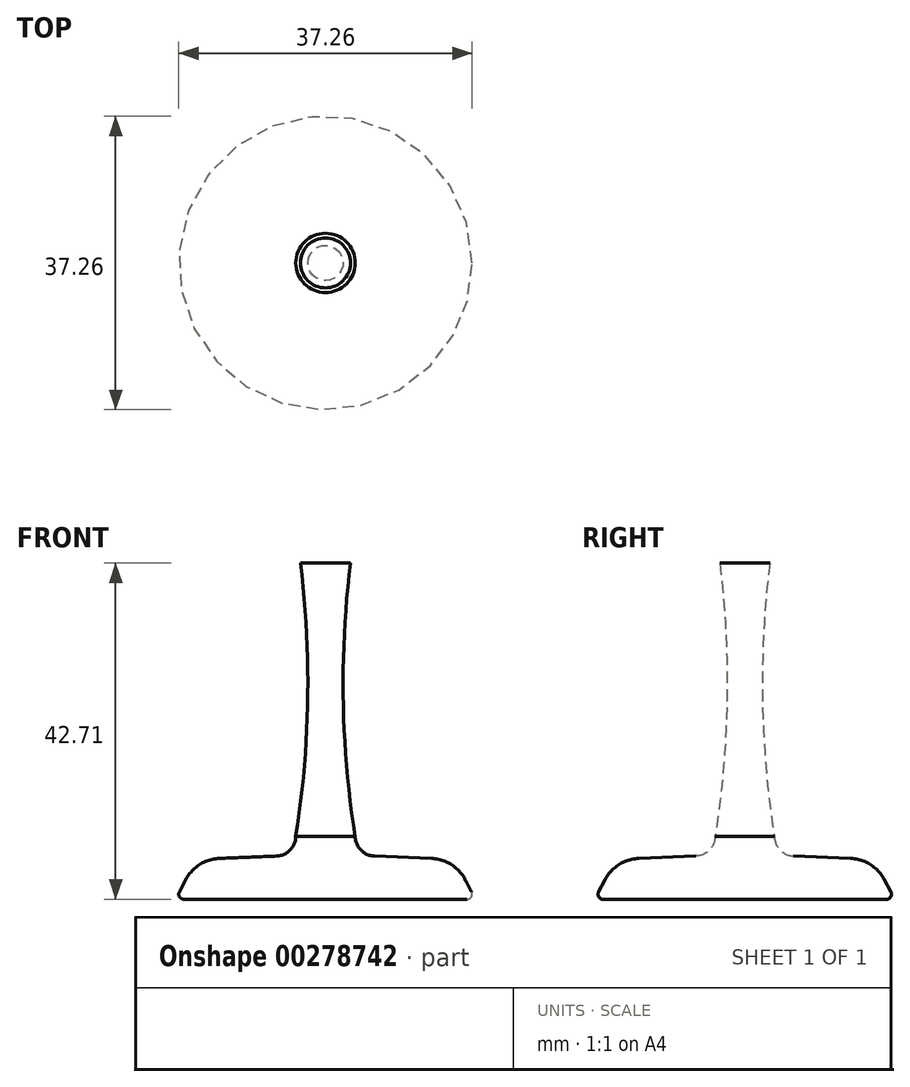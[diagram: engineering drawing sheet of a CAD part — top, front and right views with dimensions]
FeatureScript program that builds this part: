
annotation { "Feature Type Name" : "Feature", "Feature Type Description" : "" }
export const myFeature = defineFeature(function(context is Context, id is Id, definition is map)
    precondition{}
    {
        {
            var Q0;
            Q0=qCreatedBy(makeId("Front.planeOp"),FACE);
            var sketch = newSketch(context, id + "F0", { "sketchPlane" : qUnion([Q0])});
            skLineSegment(sketch, "E0", {"start": v(0, 0) * mm, "end": v(0, 50.8) * mm, "construction": true});
            skLineSegment(sketch, "E1", {"start": v(-6.2, 5.48) * mm, "end": v(-16.38, 5.08) * mm});
            skLineSegment(sketch, "E2", {"start": v(-16.38, 5.08) * mm, "end": v(-19.05, 0) * mm});
            skLineSegment(sketch, "E3", {"start": v(-19.05, 0) * mm, "end": v(0, 0) * mm});
            skLineSegment(sketch, "E4", {"start": v(0, 42.71) * mm, "end": v(-3.18, 42.71) * mm});
            skPoint(sketch, "E5.visualSharp", {"position": v(-3.81, 5.58) * mm});
            skArc(sketch, "E5.filletArc", {"start": v(-6.2, 5.48) * mm, "mid": v(-4.5, 6.24) * mm, "end": v(-3.77, 7.98) * mm});
            skLineSegment(sketch, "E6", {"start": v(0, 42.71) * mm, "end": v(0, 0) * mm});
            skArc(sketch, "E7", {"start": v(-3.77, 7.98) * mm, "mid": v(-2.26, 25.32) * mm, "end": v(-3.17, 42.71) * mm});
            skSolve(sketch);
        }
        {
            var Q0;
            Q0 = qSketchRegion(id + "F0", true);
            var Q1;
            Q1=sQuery(id+"F0.wireOp",EDGE,"E0");
            revolve(context, id + "F1", {"entities" : qUnion([Q0]), "axis" : qUnion([Q1]), "revolveType" : RevolveType.FULL});
        }
        {
            var Q0;
            Q0=makeQuery(id+"F1.opRevolve","SWEPT_EDGE",EDGE,{"disambiguationData":[OSD([sQuery(id+"F0.wireOp",EDGE,"E1"),sQuery(id+"F0.wireOp",EDGE,"E2")])]});
            fillet(context, id + "F2", {"entities" : qUnion([Q0]), "radius" : 5.08 * mm, "tangentPropagation" : true, "allowEdgeOverflow" : false});
        }
        {
            var Q0;
            Q0=makeQuery(id+"F1.opRevolve","SWEPT_EDGE",EDGE,{"disambiguationData":[OSD([sQuery(id+"F0.wireOp",EDGE,"E2"),sQuery(id+"F0.wireOp",EDGE,"E3")])]});
            fillet(context, id + "F3", {"entities" : qUnion([Q0]), "radius" : 0.64 * mm, "tangentPropagation" : true, "allowEdgeOverflow" : false});
        }
    });
